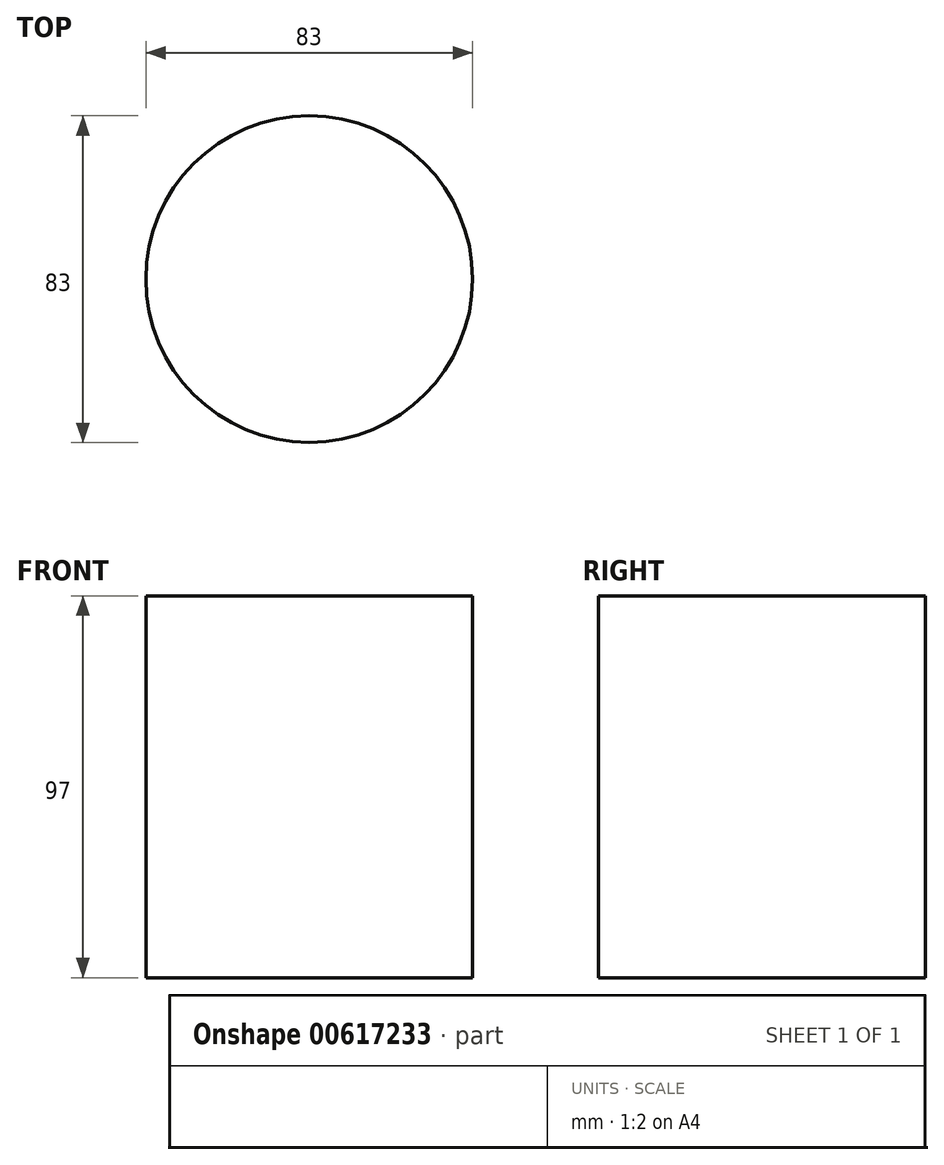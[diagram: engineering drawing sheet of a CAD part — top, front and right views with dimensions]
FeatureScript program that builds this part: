
annotation { "Feature Type Name" : "Feature", "Feature Type Description" : "" }
export const myFeature = defineFeature(function(context is Context, id is Id, definition is map)
    precondition{}
    {
        {
            var Q0;
            Q0=qCreatedBy(makeId("Top.planeOp"),FACE);
            var sketch = newSketch(context, id + "F0", { "sketchPlane" : qUnion([Q0])});
            skCircle(sketch, "E0", {"center": v(0, 0) * mm, "radius": 41.5 * mm});
            skSolve(sketch);
        }
        {
            var Q0;
            Q0 = qSketchRegion(id + "F0", true);
            extrude(context, id + "F1", {"entities" : qUnion([Q0]), "depth" : 97 * mm, "offsetDistance" : 25 * mm});
        }
        {
            var Q0;
            Q0=qCreatedBy(makeId("Right.planeOp"),FACE);
            cPlane(context, id + "F2", {"entities" : qUnion([Q0]), "cplaneType" : CPlaneType.OFFSET, "offset" : 46.5 * mm, "width" : 150 * mm, "height" : 150 * mm});
        }
    });
